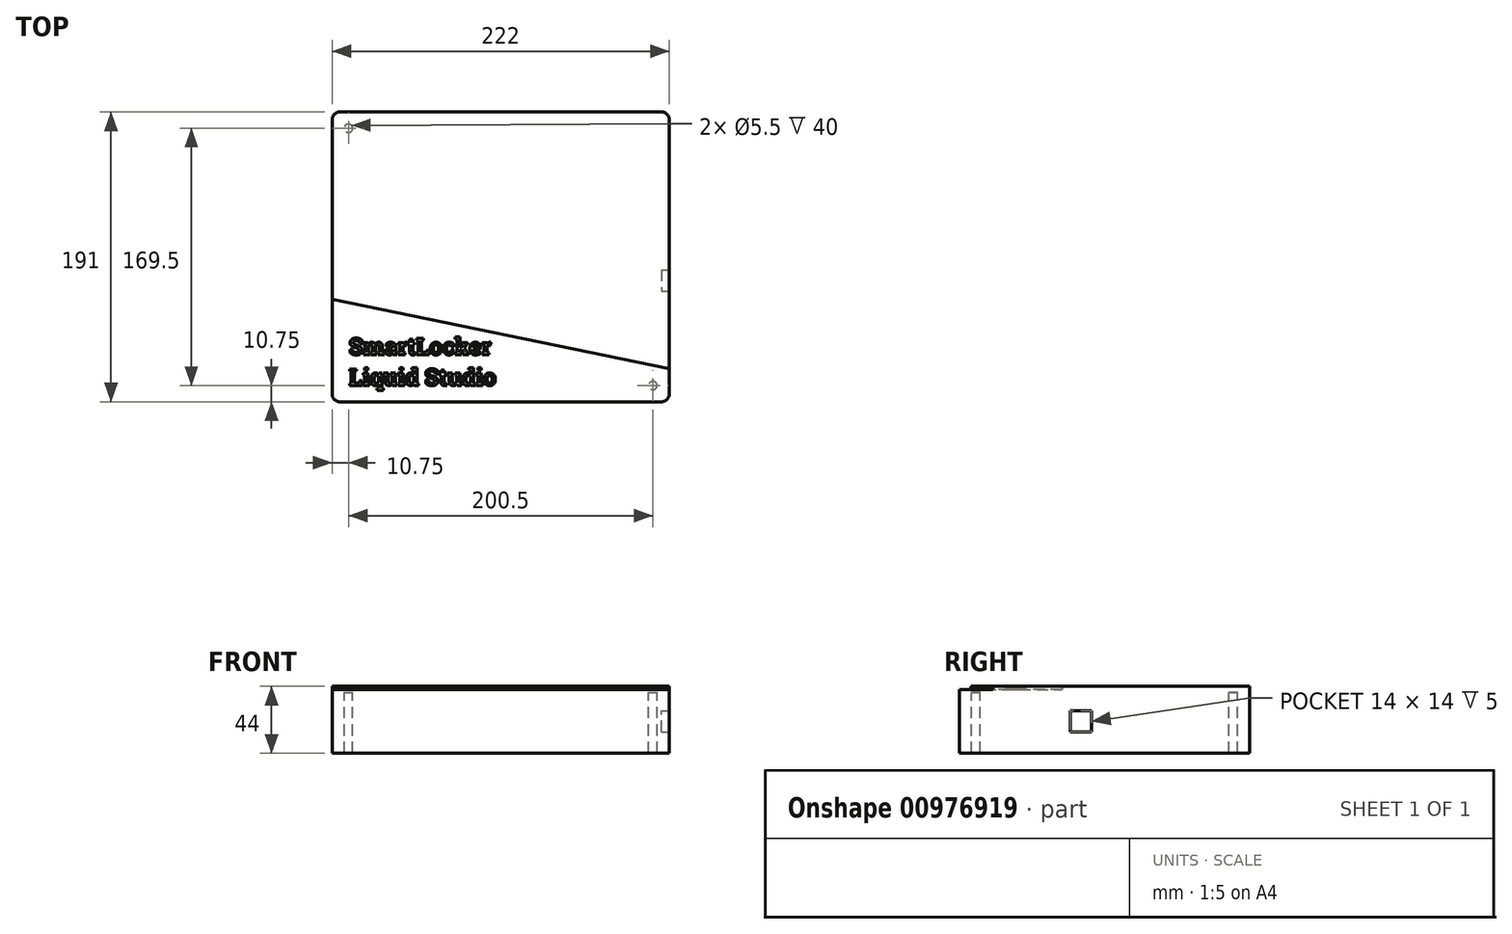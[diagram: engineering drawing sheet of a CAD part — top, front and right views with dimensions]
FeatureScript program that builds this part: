
annotation { "Feature Type Name" : "Feature", "Feature Type Description" : "" }
export const myFeature = defineFeature(function(context is Context, id is Id, definition is map)
    precondition{}
    {
        {
            var Q0;
            Q0=qCreatedBy(makeId("Top.planeOp"),FACE);
            var sketch = newSketch(context, id + "F0", { "sketchPlane" : qUnion([Q0])});
            skLineSegment(sketch, "E0.bottom", {"start": v(111, -95.5) * mm, "end": v(-111, -95.5) * mm});
            skLineSegment(sketch, "E0.top", {"start": v(111, 95.5) * mm, "end": v(-111, 95.5) * mm});
            skLineSegment(sketch, "E0.left", {"start": v(111, -95.5) * mm, "end": v(111, 95.5) * mm});
            skLineSegment(sketch, "E0.right", {"start": v(-111, -95.5) * mm, "end": v(-111, 95.5) * mm});
            skPoint(sketch, "E0.middle", {"position": v(0, 0) * mm});
            skSolve(sketch);
        }
        {
            var Q0;
            Q0=makeQuery(id+"F0.imprint","IMPRINT",FACE,{"disambiguationData":[TD([[makeQuery(id+"F0.imprint","IMPRINT",EDGE,{"derivedFrom":sQuery(id+"F0.wireOp",EDGE,"E0.bottom")}),-1.0]])]});
            extrude(context, id + "F1", {"entities" : qUnion([Q0]), "depth" : 42 * mm, "offsetDistance" : 25 * mm});
        }
        {
            var Q0;
            Q0=makeQuery(id+"F1.opExtrude","SWEPT_EDGE",EDGE,{"disambiguationData":[OSD([sQuery(id+"F0.wireOp",EDGE,"E0.bottom"),sQuery(id+"F0.wireOp",EDGE,"E0.left")])]});
            var Q1;
            Q1=makeQuery(id+"F1.opExtrude","SWEPT_EDGE",EDGE,{"disambiguationData":[OSD([sQuery(id+"F0.wireOp",EDGE,"E0.top"),sQuery(id+"F0.wireOp",EDGE,"E0.left")])]});
            var Q2;
            Q2=makeQuery(id+"F1.opExtrude","SWEPT_EDGE",EDGE,{"disambiguationData":[OSD([sQuery(id+"F0.wireOp",EDGE,"E0.bottom"),sQuery(id+"F0.wireOp",EDGE,"E0.right")])]});
            var Q3;
            Q3=makeQuery(id+"F1.opExtrude","SWEPT_EDGE",EDGE,{"disambiguationData":[OSD([sQuery(id+"F0.wireOp",EDGE,"E0.top"),sQuery(id+"F0.wireOp",EDGE,"E0.right")])]});
            fillet(context, id + "F2", {"entities" : qUnion([Q0, Q1, Q2, Q3]), "radius" : 5 * mm, "tangentPropagation" : true, "allowEdgeOverflow" : false});
        }
        {
            var Q0;
            Q0=makeQuery(id+"F1.opExtrude","CAP_FACE",FACE,{"disambiguationData":[OSD([sQuery(id+"F0.wireOp",EDGE,"E0.bottom"),sQuery(id+"F0.wireOp",EDGE,"E0.top"),sQuery(id+"F0.wireOp",EDGE,"E0.left"),sQuery(id+"F0.wireOp",EDGE,"E0.right")])],"isStart":false});
            var sketch = newSketch(context, id + "F3", { "sketchPlane" : qUnion([Q0])});
            skText(sketch, "E1", { "text": "SmartLocker\nLiquid Studio", "fontName": "RobotoSlab-Bold.ttf"});
            const initialGuessF3  = {"E1": [-0.1, -0.0645, 1, 0, 0.01103]};
            skSetInitialGuess(sketch, initialGuessF3);
            skSolve(sketch);
        }
        {
            var Q0;
            Q0=qSketchRegion(id+"F3",true);
            extrude(context, id + "F4", {"entities" : qUnion([Q0]), "operationType" : NewBodyOperationType.ADD, "depth" : 2 * mm, "offsetDistance" : 25 * mm});
        }
        {
            var Q0;
            Q0=makeQuery(id+"F1.opExtrude","CAP_FACE",FACE,{"disambiguationData":[OSD([sQuery(id+"F0.wireOp",EDGE,"E0.bottom"),sQuery(id+"F0.wireOp",EDGE,"E0.top"),sQuery(id+"F0.wireOp",EDGE,"E0.left"),sQuery(id+"F0.wireOp",EDGE,"E0.right")])],"isStart":true});
            var sketch = newSketch(context, id + "F5", { "sketchPlane" : qUnion([Q0])});
            skLineSegment(sketch, "E2.0", {"start": v(-105, -92.5) * mm, "end": v(105, -92.5) * mm});
            skLineSegment(sketch, "E2.1", {"start": v(-108, 89.5) * mm, "end": v(-108, -89.5) * mm});
            skLineSegment(sketch, "E2.2", {"start": v(105, 92.5) * mm, "end": v(-105, 92.5) * mm});
            skLineSegment(sketch, "E2.3", {"start": v(108, -89.5) * mm, "end": v(108, 89.5) * mm});
            skPoint(sketch, "E3.visualSharp", {"position": v(-108, -92.5) * mm});
            skArc(sketch, "E3.filletArc", {"start": v(-108, -89.5) * mm, "mid": v(-107.12, -91.62) * mm, "end": v(-105, -92.5) * mm});
            skPoint(sketch, "E4.visualSharp", {"position": v(108, -92.5) * mm});
            skArc(sketch, "E4.filletArc", {"start": v(105, -92.5) * mm, "mid": v(107.12, -91.62) * mm, "end": v(108, -89.5) * mm});
            skPoint(sketch, "E5.visualSharp", {"position": v(108, 92.5) * mm});
            skArc(sketch, "E5.filletArc", {"start": v(108, 89.5) * mm, "mid": v(107.12, 91.62) * mm, "end": v(105, 92.5) * mm});
            skPoint(sketch, "E6.visualSharp", {"position": v(-108, 92.5) * mm});
            skArc(sketch, "E6.filletArc", {"start": v(-105, 92.5) * mm, "mid": v(-107.12, 91.62) * mm, "end": v(-108, 89.5) * mm});
            skSolve(sketch);
        }
        {
            var Q0;
            Q0=makeQuery(id+"F5.imprint","IMPRINT",FACE,{"disambiguationData":[TD([[makeQuery(id+"F5.imprint","IMPRINT",EDGE,{"derivedFrom":sQuery(id+"F5.wireOp",EDGE,"E2.0")}),1.0]])]});
            extrude(context, id + "F6", {"entities" : qUnion([Q0]), "operationType" : NewBodyOperationType.REMOVE, "oppositeDirection" : true, "depth" : 40 * mm, "offsetDistance" : 25 * mm});
        }
        {
            var Q0;
            Q0=makeQuery(id+"F6.boolean.opBoolean","COPY",FACE,{"derivedFrom":makeQuery(id+"F6.opExtrude","CAP_FACE",FACE,{"disambiguationData":[OSD([sQuery(id+"F5.wireOp",EDGE,"E2.0"),sQuery(id+"F5.wireOp",EDGE,"E2.1"),sQuery(id+"F5.wireOp",EDGE,"E2.2"),sQuery(id+"F5.wireOp",EDGE,"E2.3")])],"isStart":false})});
            var sketch = newSketch(context, id + "F7", { "sketchPlane" : qUnion([Q0])});
            skCircle(sketch, "E7", {"center": v(-100.25, 84.75) * mm, "radius": 2.75 * mm});
            skCircle(sketch, "E8.MirrorC", {"center": v(100.25, 84.75) * mm, "radius": 2.75 * mm});
            skCircle(sketch, "E9.MirrorC", {"center": v(-100.25, -84.75) * mm, "radius": 2.75 * mm});
            skCircle(sketch, "E10.MirrorC", {"center": v(100.25, -84.75) * mm, "radius": 2.75 * mm});
            skCircle(sketch, "E11", {"center": v(0, -84.75) * mm, "radius": 2.75 * mm});
            skSolve(sketch);
        }
        {
            var Q0;
            Q0=makeQuery(id+"F7.imprint","IMPRINT",FACE,{"disambiguationData":[TD([[makeQuery(id+"F7.imprint","IMPRINT",EDGE,{"derivedFrom":sQuery(id+"F7.wireOp",EDGE,"E7")}),1.0]])]});
            var Q1;
            Q1=makeQuery(id+"F7.imprint","IMPRINT",FACE,{"disambiguationData":[TD([[makeQuery(id+"F7.imprint","IMPRINT",EDGE,{"derivedFrom":sQuery(id+"F7.wireOp",EDGE,"E8.MirrorC")}),-1.0]])]});
            var Q2;
            Q2=makeQuery(id+"F7.imprint","IMPRINT",FACE,{"disambiguationData":[TD([[makeQuery(id+"F7.imprint","IMPRINT",EDGE,{"derivedFrom":sQuery(id+"F7.wireOp",EDGE,"E10.MirrorC")}),1.0]])]});
            var Q3;
            Q3=makeQuery(id+"F7.imprint","IMPRINT",FACE,{"disambiguationData":[TD([[makeQuery(id+"F7.imprint","IMPRINT",EDGE,{"derivedFrom":sQuery(id+"F7.wireOp",EDGE,"E9.MirrorC")}),-1.0]])]});
            var Q4;
            Q4=makeQuery(id+"F7.imprint","IMPRINT",FACE,{"disambiguationData":[TD([[makeQuery(id+"F7.imprint","IMPRINT",EDGE,{"derivedFrom":sQuery(id+"F7.wireOp",EDGE,"E11")}),1.0]])]});
            var Q5;
            Q5=makeQuery(id+"F7.imprint","IMPRINT",FACE,{"disambiguationData":[TD([[makeQuery(id+"F7.imprint","IMPRINT",EDGE,{"derivedFrom":sQuery(id+"F7.wireOp",EDGE,"S0v4FPnU-rghZ-5bN9-Dwdb-Z3T0p1FfuOBr")}),1.0]])]});
            extrude(context, id + "F8", {"entities" : qUnion([Q0, Q1, Q2, Q3, Q4, Q5]), "operationType" : NewBodyOperationType.ADD, "depth" : 40 * mm, "offsetDistance" : 25 * mm});
        }
        {
            var Q0;
            Q0=makeQuery(id+"F6.boolean.opBoolean","COPY",FACE,{"derivedFrom":makeQuery(id+"F6.opExtrude","CAP_FACE",FACE,{"disambiguationData":[OSD([sQuery(id+"F5.wireOp",EDGE,"E2.0"),sQuery(id+"F5.wireOp",EDGE,"E2.1"),sQuery(id+"F5.wireOp",EDGE,"E2.2"),sQuery(id+"F5.wireOp",EDGE,"E2.3"),sQuery(id+"F5.wireOp",EDGE,"E3.filletArc"),sQuery(id+"F5.wireOp",EDGE,"E4.filletArc"),sQuery(id+"F5.wireOp",EDGE,"E5.filletArc"),sQuery(id+"F5.wireOp",EDGE,"E6.filletArc")])],"isStart":false})});
            var sketch = newSketch(context, id + "F9", { "sketchPlane" : qUnion([Q0])});
            skCircle(sketch, "E12", {"center": v(-63, -15.5) * mm, "radius": 4 * mm});
            skCircle(sketch, "E13", {"center": v(73, -5.5) * mm, "radius": 4 * mm});
            skCircle(sketch, "E14", {"center": v(0, -32.5) * mm, "radius": 4 * mm});
            skSolve(sketch);
        }
        {
            var Q0;
            Q0=makeQuery(id+"F9.imprint","IMPRINT",FACE,{"disambiguationData":[TD([[makeQuery(id+"F9.imprint","IMPRINT",EDGE,{"derivedFrom":sQuery(id+"F9.wireOp",EDGE,"E12")}),1.0]])]});
            var Q1;
            Q1=makeQuery(id+"F9.imprint","IMPRINT",FACE,{"disambiguationData":[TD([[makeQuery(id+"F9.imprint","IMPRINT",EDGE,{"derivedFrom":sQuery(id+"F9.wireOp",EDGE,"E13")}),1.0]])]});
            var Q2;
            Q2=makeQuery(id+"F9.imprint","IMPRINT",FACE,{"disambiguationData":[TD([[makeQuery(id+"F9.imprint","IMPRINT",EDGE,{"derivedFrom":sQuery(id+"F9.wireOp",EDGE,"E14")}),1.0]])]});
            extrude(context, id + "F10", {"entities" : qUnion([Q0, Q1, Q2]), "operationType" : NewBodyOperationType.ADD, "depth" : 11 * mm, "offsetDistance" : 25 * mm});
        }
        {
            var Q0;
            {var subQ0=sQuery(id+"F0.wireOp",EDGE,"E0.right");var subQ1=sQuery(id+"F0.wireOp",EDGE,"E0.top");var subQ2=sQuery(id+"F0.wireOp",EDGE,"E0.left");var subQ3=sQuery(id+"F0.wireOp",EDGE,"E0.bottom");Q0=makeQuery(id+"F4.boolean.opBoolean","SPLIT",FACE,{"disambiguationData":[TD([makeQuery(id+"F1.opExtrude","SWEPT_FACE",FACE,{"disambiguationData":[OSD([subQ3])]})])],"derivedFrom":makeQuery(id+"F1.opExtrude","CAP_FACE",FACE,{"disambiguationData":[OSD([subQ3,subQ1,subQ2,subQ0])],"isStart":false})});}
            cPlane(context, id + "F11", {"entities" : qUnion([Q0]), "cplaneType" : CPlaneType.OFFSET, "offset" : 10 * mm, "width" : 150 * mm, "height" : 150 * mm});
        }
        {
            var Q0;
            Q0=qCreatedBy(id+"F11.planeOp",FACE);
            var sketch = newSketch(context, id + "F12", { "sketchPlane" : qUnion([Q0])});
            skPoint(sketch, "E15", {"position": v(-51.1, 51.77) * mm});
            skSolve(sketch);
        }
        {
            var Q0;
            {var subQ0=sQuery(id+"F0.wireOp",EDGE,"E0.right");var subQ1=sQuery(id+"F0.wireOp",EDGE,"E0.top");var subQ2=sQuery(id+"F0.wireOp",EDGE,"E0.left");var subQ3=sQuery(id+"F0.wireOp",EDGE,"E0.bottom");Q0=makeQuery(id+"F4.boolean.opBoolean","SPLIT",FACE,{"disambiguationData":[TD([makeQuery(id+"F1.opExtrude","SWEPT_FACE",FACE,{"disambiguationData":[OSD([subQ3])]})])],"derivedFrom":makeQuery(id+"F1.opExtrude","CAP_FACE",FACE,{"disambiguationData":[OSD([subQ3,subQ1,subQ2,subQ0])],"isStart":false})});}
            var sketch = newSketch(context, id + "F13", { "sketchPlane" : qUnion([Q0])});
            skLineSegment(sketch, "E16.0", {"start": v(-111, -27.94) * mm, "end": v(-111, 89.5) * mm});
            skLineSegment(sketch, "E16.1", {"start": v(111, -73.7) * mm, "end": v(111, 89.5) * mm});
            skArc(sketch, "E16.2", {"start": v(111, 89.5) * mm, "mid": v(109.66, 94.16) * mm, "end": v(105, 95.5) * mm});
            skLineSegment(sketch, "E16.3", {"start": v(105, 95.5) * mm, "end": v(-105, 95.5) * mm});
            skArc(sketch, "E16.4", {"start": v(-105, 95.5) * mm, "mid": v(-109.66, 94.16) * mm, "end": v(-111, 89.5) * mm});
            skLineSegment(sketch, "E17", {"start": v(-111, -27.94) * mm, "end": v(111, -73.7) * mm});
            skSolve(sketch);
        }
        {
            var Q0;
            Q0=makeQuery(id+"F13.imprint","IMPRINT",FACE,{"disambiguationData":[TD([[makeQuery(id+"F13.imprint","IMPRINT",EDGE,{"derivedFrom":sQuery(id+"F13.wireOp",EDGE,"E16.0")}),-1.0]])]});
            extrude(context, id + "F14", {"entities" : qUnion([Q0]), "operationType" : NewBodyOperationType.ADD, "depth" : 2 * mm, "offsetDistance" : 25 * mm});
        }
        {
            var Q0;
            Q0=makeQuery(id+"F14.boolean.opBoolean","MERGE",FACE,{"derivedFrom":[makeQuery(id+"F1.opExtrude","SWEPT_FACE",FACE,{"disambiguationData":[OSD([sQuery(id+"F0.wireOp",EDGE,"E0.left")])]}),makeQuery(id+"F14.opExtrude","SWEPT_FACE",FACE,{"disambiguationData":[OSD([sQuery(id+"F13.wireOp",EDGE,"E16.1")])]})]});
            var sketch = newSketch(context, id + "F15", { "sketchPlane" : qUnion([Q0])});
            skLineSegment(sketch, "E18.bottom", {"start": v(-8.5, 14) * mm, "end": v(-22.5, 14) * mm});
            skLineSegment(sketch, "E18.top", {"start": v(-8.5, 28) * mm, "end": v(-22.5, 28) * mm});
            skLineSegment(sketch, "E18.left", {"start": v(-8.5, 14) * mm, "end": v(-8.5, 28) * mm});
            skLineSegment(sketch, "E18.right", {"start": v(-22.5, 14) * mm, "end": v(-22.5, 28) * mm});
            skPoint(sketch, "E18.middle", {"position": v(-15.5, 21) * mm});
            skSolve(sketch);
        }
        {
            var Q0;
            Q0=makeQuery(id+"F15.imprint","IMPRINT",FACE,{"disambiguationData":[TD([[makeQuery(id+"F15.imprint","IMPRINT",EDGE,{"derivedFrom":sQuery(id+"F15.wireOp",EDGE,"E18.bottom")}),-1.0]])]});
            extrude(context, id + "F16", {"entities" : qUnion([Q0]), "operationType" : NewBodyOperationType.REMOVE, "oppositeDirection" : true, "depth" : 5 * mm, "offsetDistance" : 25 * mm});
        }
    });
